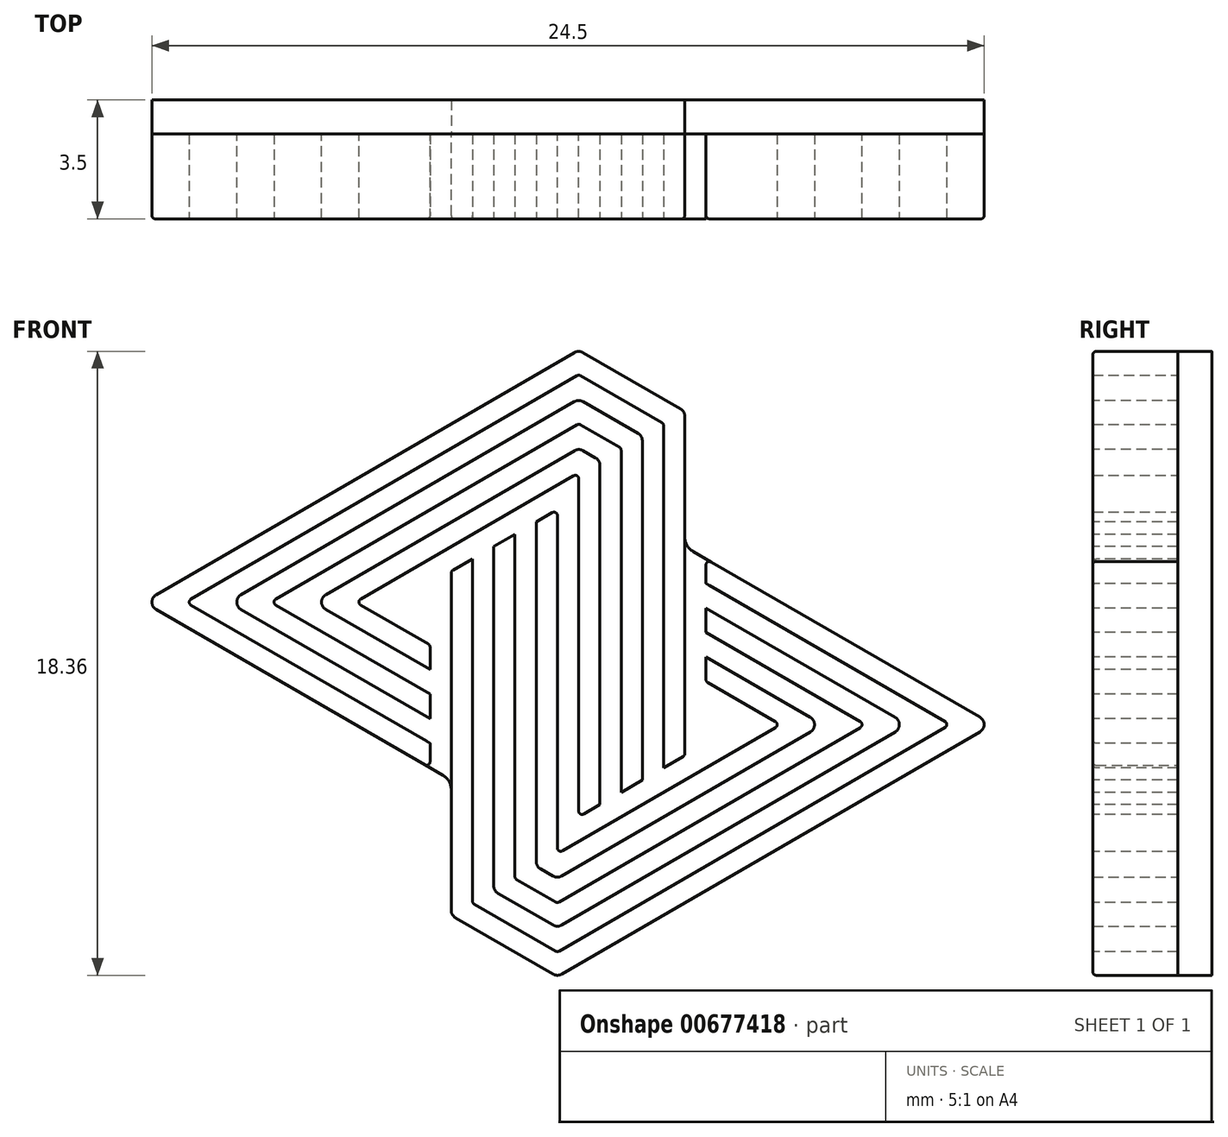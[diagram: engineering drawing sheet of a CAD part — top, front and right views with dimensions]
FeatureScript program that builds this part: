
annotation { "Feature Type Name" : "Feature", "Feature Type Description" : "" }
export const myFeature = defineFeature(function(context is Context, id is Id, definition is map)
    precondition{}
    {
        {
            var Q0;
            Q0=qCreatedBy(makeId("Front.planeOp"),FACE);
            var sketch = newSketch(context, id + "F0", { "sketchPlane" : qUnion([Q0])});
            skLineSegment(sketch, "E0.bottom", {"start": v(-12.5, 9.22) * mm, "end": v(12.5, 9.22) * mm, "construction": true});
            skLineSegment(sketch, "E0.top", {"start": v(-12.5, -9.22) * mm, "end": v(12.5, -9.22) * mm, "construction": true});
            skLineSegment(sketch, "E0.left", {"start": v(-12.5, 9.22) * mm, "end": v(-12.5, -9.22) * mm, "construction": true});
            skLineSegment(sketch, "E0.right", {"start": v(12.5, 9.22) * mm, "end": v(12.5, -9.22) * mm, "construction": true});
            skLineSegment(sketch, "E1", {"start": v(0, 9.22) * mm, "end": v(0, -9.22) * mm, "construction": true});
            skLineSegment(sketch, "E2", {"start": v(-3.44, 9.22) * mm, "end": v(-3.44, -9.22) * mm, "construction": true});
            skLineSegment(sketch, "E3.MirrorCS", {"start": v(3.44, 9.22) * mm, "end": v(3.44, -9.22) * mm, "construction": true});
            skLineSegment(sketch, "E4", {"start": v(-12.5, 1.8) * mm, "end": v(-3.44, 1.8) * mm, "construction": true});
            skLineSegment(sketch, "E5", {"start": v(3.44, -1.8) * mm, "end": v(12.5, -1.8) * mm, "construction": true});
            skLineSegment(sketch, "E6", {"start": v(-0.31, 0) * mm, "end": v(-0.31, -9.22) * mm, "construction": true});
            skLineSegment(sketch, "E7", {"start": v(-3.44, -7.42) * mm, "end": v(0, -7.42) * mm, "construction": true});
            skLineSegment(sketch, "E8", {"start": v(0, 7.42) * mm, "end": v(3.44, 7.42) * mm, "construction": true});
            skLineSegment(sketch, "E9", {"start": v(-4.06, -9.22) * mm, "end": v(-4.06, 1.8) * mm, "construction": true});
            skLineSegment(sketch, "E10", {"start": v(0.31, 0) * mm, "end": v(0.31, 9.22) * mm, "construction": true});
            skLineSegment(sketch, "E11", {"start": v(-12.5, 1.8) * mm, "end": v(0.31, 9.22) * mm});
            skLineSegment(sketch, "E12", {"start": v(0.31, 9.22) * mm, "end": v(3.44, 7.42) * mm});
            skLineSegment(sketch, "E13", {"start": v(-0.31, -9.22) * mm, "end": v(-3.44, -7.42) * mm});
            skLineSegment(sketch, "E14", {"start": v(-0.31, -9.22) * mm, "end": v(12.5, -1.8) * mm});
            skLineSegment(sketch, "E15", {"start": v(-12.5, 1.8) * mm, "end": v(-4.06, -3.07) * mm});
            skLineSegment(sketch, "E16", {"start": v(-3.44, -7.42) * mm, "end": v(-3.44, 1.8) * mm});
            skLineSegment(sketch, "E17.MirrorCS", {"start": v(4.06, -9.22) * mm, "end": v(4.06, 1.8) * mm, "construction": true});
            skLineSegment(sketch, "E18", {"start": v(4.06, 1.8) * mm, "end": v(4.06, 5.32) * mm, "construction": true});
            skLineSegment(sketch, "E19", {"start": v(12.5, -1.8) * mm, "end": v(4.06, 3.07) * mm});
            skLineSegment(sketch, "E20.0", {"start": v(-6.26, 1.8) * mm, "end": v(-4.06, 0.54) * mm});
            skLineSegment(sketch, "E21.trimOffspring", {"start": v(-6.26, 1.8) * mm, "end": v(0.31, 5.6) * mm});
            skLineSegment(sketch, "E22.0", {"start": v(6.26, -1.8) * mm, "end": v(4.06, -0.54) * mm});
            skLineSegment(sketch, "E22.1", {"start": v(-0.31, -5.6) * mm, "end": v(6.26, -1.8) * mm});
            skLineSegment(sketch, "E23", {"start": v(-2.2, 4.16) * mm, "end": v(-1.88, 3.62) * mm, "construction": true});
            skLineSegment(sketch, "E24.0", {"start": v(-3.44, 2.71) * mm, "end": v(-0.31, 4.52) * mm});
            skLineSegment(sketch, "E25", {"start": v(-3.44, 2.71) * mm, "end": v(-3.44, 1.8) * mm});
            skLineSegment(sketch, "E26.0", {"start": v(0.31, -4.52) * mm, "end": v(3.44, -2.71) * mm});
            skPoint(sketch, "E27.orphan", {"position": v(1.88, 6.51) * mm});
            skLineSegment(sketch, "E28", {"start": v(3.44, 7.42) * mm, "end": v(3.44, -2.71) * mm});
            skLineSegment(sketch, "E29", {"start": v(0.31, -4.52) * mm, "end": v(0.31, 5.6) * mm});
            skLineSegment(sketch, "E30", {"start": v(-0.31, 4.52) * mm, "end": v(-0.31, -5.6) * mm});
            skLineSegment(sketch, "E31", {"start": v(-4.06, -3.07) * mm, "end": v(-4.06, 0.54) * mm});
            skLineSegment(sketch, "E32", {"start": v(4.06, 3.07) * mm, "end": v(4.06, -0.54) * mm});
            skSolve(sketch);
        }
        {
            var Q0;
            Q0 = qSketchRegion(id + "F0", true);
            extrude(context, id + "F1", {"entities" : qUnion([Q0]), "depth" : 2.5 * mm, "offsetDistance" : 25 * mm});
        }
        {
            var Q0;
            Q0=makeQuery(id+"F1.opExtrude","CAP_FACE",FACE,{"disambiguationData":[OSD([sQuery(id+"F0.wireOp",EDGE,"E11"),sQuery(id+"F0.wireOp",EDGE,"E12"),sQuery(id+"F0.wireOp",EDGE,"E15"),sQuery(id+"F0.wireOp",EDGE,"E20.0"),sQuery(id+"F0.wireOp",EDGE,"E21.trimOffspring"),sQuery(id+"F0.wireOp",EDGE,"E26.0"),sQuery(id+"F0.wireOp",EDGE,"E28"),sQuery(id+"F0.wireOp",EDGE,"E29"),sQuery(id+"F0.wireOp",EDGE,"E31")])],"isStart":false});
            var sketch = newSketch(context, id + "F2", { "sketchPlane" : qUnion([Q0])});
            skLineSegment(sketch, "E33.0", {"start": v(-11.25, 1.8) * mm, "end": v(-4.06, -2.35) * mm});
            skLineSegment(sketch, "E34.0", {"start": v(-11.25, 1.8) * mm, "end": v(0.31, 8.5) * mm});
            skLineSegment(sketch, "E35.0", {"start": v(2.81, 7.06) * mm, "end": v(2.81, -3.08) * mm});
            skLineSegment(sketch, "E35.1", {"start": v(0.31, 8.5) * mm, "end": v(2.81, 7.06) * mm});
            skLineSegment(sketch, "E36.0", {"start": v(-10, 1.8) * mm, "end": v(-4.06, -1.63) * mm});
            skLineSegment(sketch, "E36.1", {"start": v(-10, 1.8) * mm, "end": v(0.31, 7.78) * mm});
            skLineSegment(sketch, "E36.2", {"start": v(0.31, 7.78) * mm, "end": v(2.19, 6.7) * mm});
            skLineSegment(sketch, "E36.3", {"start": v(2.19, 6.7) * mm, "end": v(2.19, -3.44) * mm});
            skLineSegment(sketch, "E37", {"start": v(-4.06, -2.35) * mm, "end": v(-4.06, -1.63) * mm});
            skLineSegment(sketch, "E38", {"start": v(2.19, -3.44) * mm, "end": v(2.81, -3.08) * mm});
            skLineSegment(sketch, "E39.0", {"start": v(-8.75, 1.8) * mm, "end": v(-4.06, -0.9) * mm});
            skLineSegment(sketch, "E39.1", {"start": v(-8.75, 1.8) * mm, "end": v(0.32, 7.05) * mm});
            skLineSegment(sketch, "E39.2", {"start": v(0.32, 7.05) * mm, "end": v(1.56, 6.34) * mm});
            skLineSegment(sketch, "E39.3", {"start": v(1.56, 6.34) * mm, "end": v(1.56, -3.8) * mm});
            skLineSegment(sketch, "E40.0", {"start": v(-7.5, 1.8) * mm, "end": v(-4.06, -0.18) * mm});
            skLineSegment(sketch, "E40.1", {"start": v(-7.5, 1.8) * mm, "end": v(0.32, 6.33) * mm});
            skLineSegment(sketch, "E40.2", {"start": v(0.32, 6.33) * mm, "end": v(0.94, 5.97) * mm});
            skLineSegment(sketch, "E40.3", {"start": v(0.94, 5.97) * mm, "end": v(0.94, -4.16) * mm});
            skLineSegment(sketch, "E41", {"start": v(-4.06, -0.9) * mm, "end": v(-4.06, -0.18) * mm});
            skLineSegment(sketch, "E42", {"start": v(0.94, -4.16) * mm, "end": v(1.56, -3.8) * mm});
            skSolve(sketch);
        }
        {
            var Q0;
            Q0 = qSketchRegion(id + "F2", true);
            extrude(context, id + "F3", {"entities" : qUnion([Q0]), "operationType" : NewBodyOperationType.REMOVE, "oppositeDirection" : true, "depth" : 25 * mm, "offsetDistance" : 25 * mm});
        }
        {
            var Q0;
            Q0=makeQuery(id+"F1.opExtrude","CAP_FACE",FACE,{"disambiguationData":[OSD([sQuery(id+"F0.wireOp",EDGE,"E13"),sQuery(id+"F0.wireOp",EDGE,"E14"),sQuery(id+"F0.wireOp",EDGE,"E16"),sQuery(id+"F0.wireOp",EDGE,"E19"),sQuery(id+"F0.wireOp",EDGE,"E22.0"),sQuery(id+"F0.wireOp",EDGE,"E22.1"),sQuery(id+"F0.wireOp",EDGE,"E24.0"),sQuery(id+"F0.wireOp",EDGE,"E25"),sQuery(id+"F0.wireOp",EDGE,"E30"),sQuery(id+"F0.wireOp",EDGE,"E32")])],"isStart":false});
            var sketch = newSketch(context, id + "F4", { "sketchPlane" : qUnion([Q0])});
            skLineSegment(sketch, "E43.0", {"start": v(11.25, -1.8) * mm, "end": v(4.06, 2.35) * mm});
            skLineSegment(sketch, "E43.1", {"start": v(-2.81, 3.08) * mm, "end": v(-2.81, 1.8) * mm});
            skLineSegment(sketch, "E43.2", {"start": v(-2.81, -7.06) * mm, "end": v(-2.81, 1.8) * mm});
            skLineSegment(sketch, "E43.3", {"start": v(-0.31, -8.5) * mm, "end": v(-2.81, -7.06) * mm});
            skLineSegment(sketch, "E43.4", {"start": v(-0.31, -8.5) * mm, "end": v(11.25, -1.8) * mm});
            skLineSegment(sketch, "E44.0", {"start": v(10, -1.8) * mm, "end": v(4.06, 1.63) * mm});
            skLineSegment(sketch, "E44.1", {"start": v(-2.19, 3.44) * mm, "end": v(-2.19, 1.8) * mm});
            skLineSegment(sketch, "E44.2", {"start": v(-2.19, -6.7) * mm, "end": v(-2.19, 1.8) * mm});
            skLineSegment(sketch, "E44.3", {"start": v(-0.31, -7.78) * mm, "end": v(-2.19, -6.7) * mm});
            skLineSegment(sketch, "E44.4", {"start": v(-0.31, -7.78) * mm, "end": v(10, -1.8) * mm});
            skLineSegment(sketch, "E45", {"start": v(-2.81, 3.08) * mm, "end": v(-2.19, 3.44) * mm});
            skLineSegment(sketch, "E46", {"start": v(4.06, 1.63) * mm, "end": v(4.06, 2.35) * mm});
            skLineSegment(sketch, "E47.0", {"start": v(8.75, -1.8) * mm, "end": v(4.06, 0.9) * mm});
            skLineSegment(sketch, "E47.1", {"start": v(-1.56, 3.8) * mm, "end": v(-1.56, 1.8) * mm});
            skLineSegment(sketch, "E47.2", {"start": v(-1.56, -6.33) * mm, "end": v(-1.56, 1.8) * mm});
            skLineSegment(sketch, "E47.3", {"start": v(-0.31, -7.05) * mm, "end": v(-1.56, -6.33) * mm});
            skLineSegment(sketch, "E47.4", {"start": v(-0.31, -7.05) * mm, "end": v(8.75, -1.8) * mm});
            skLineSegment(sketch, "E48.0", {"start": v(7.5, -1.8) * mm, "end": v(4.06, 0.18) * mm});
            skLineSegment(sketch, "E48.1", {"start": v(-0.94, 4.16) * mm, "end": v(-0.94, 1.8) * mm});
            skLineSegment(sketch, "E48.2", {"start": v(-0.94, -5.97) * mm, "end": v(-0.94, 1.8) * mm});
            skLineSegment(sketch, "E48.3", {"start": v(-0.32, -6.33) * mm, "end": v(-0.94, -5.97) * mm});
            skLineSegment(sketch, "E48.4", {"start": v(-0.32, -6.33) * mm, "end": v(7.5, -1.8) * mm});
            skLineSegment(sketch, "E49", {"start": v(-1.56, 3.8) * mm, "end": v(-0.94, 4.16) * mm});
            skLineSegment(sketch, "E50", {"start": v(4.06, 0.18) * mm, "end": v(4.06, 0.9) * mm});
            skSolve(sketch);
        }
        {
            var Q0;
            Q0 = qSketchRegion(id + "F4", true);
            extrude(context, id + "F5", {"entities" : qUnion([Q0]), "operationType" : NewBodyOperationType.REMOVE, "oppositeDirection" : true, "depth" : 25 * mm, "offsetDistance" : 25 * mm});
        }
        {
            var Q0;
            {var subQ0=sQuery(id+"F0.wireOp",EDGE,"E19");var subQ1=sQuery(id+"F0.wireOp",EDGE,"E32");var subQ2=sQuery(id+"F0.wireOp",EDGE,"E14");var subQ3=sQuery(id+"F0.wireOp",EDGE,"E25");var subQ4=sQuery(id+"F0.wireOp",EDGE,"E16");var subQ5=sQuery(id+"F0.wireOp",EDGE,"E13");var subQ6=sQuery(id+"F0.wireOp",EDGE,"E24.0");Q0=makeQuery(id+"F5.boolean.opBoolean","SPLIT",FACE,{"disambiguationData":[TD([makeQuery(id+"F1.opExtrude","SWEPT_FACE",FACE,{"disambiguationData":[OSD([subQ5])]})])],"derivedFrom":makeQuery(id+"F1.opExtrude","CAP_FACE",FACE,{"disambiguationData":[OSD([subQ5,subQ2,subQ4,subQ0,sQuery(id+"F0.wireOp",EDGE,"E22.0"),sQuery(id+"F0.wireOp",EDGE,"E22.1"),subQ6,subQ3,sQuery(id+"F0.wireOp",EDGE,"E30"),subQ1])],"isStart":true})});}
            var sketch = newSketch(context, id + "F6", { "sketchPlane" : qUnion([Q0])});
            skLineSegment(sketch, "E51.0", {"start": v(-12.5, -1.8) * mm, "end": v(-4.06, 3.07) * mm});
            skLineSegment(sketch, "E51.1", {"start": v(0.31, -9.22) * mm, "end": v(-12.5, -1.8) * mm});
            skLineSegment(sketch, "E51.2", {"start": v(0.31, -9.22) * mm, "end": v(3.44, -7.42) * mm});
            skLineSegment(sketch, "E51.3", {"start": v(3.44, -3.43) * mm, "end": v(3.44, -7.42) * mm});
            skLineSegment(sketch, "E51.4", {"start": v(12.5, 1.8) * mm, "end": v(4.06, -3.07) * mm});
            skLineSegment(sketch, "E51.5", {"start": v(-3.44, 7.42) * mm, "end": v(-3.44, 3.43) * mm});
            skLineSegment(sketch, "E51.6", {"start": v(-0.31, 9.22) * mm, "end": v(-3.44, 7.42) * mm});
            skLineSegment(sketch, "E51.7", {"start": v(12.5, 1.8) * mm, "end": v(-0.31, 9.22) * mm});
            skPoint(sketch, "E51.8", {"position": v(1.87, -8.32) * mm});
            skLineSegment(sketch, "E52", {"start": v(-4.06, 3.07) * mm, "end": v(-3.44, 3.43) * mm});
            skLineSegment(sketch, "E53", {"start": v(4.06, -3.07) * mm, "end": v(3.44, -3.43) * mm});
            skPoint(sketch, "E54.orphan", {"position": v(-3.44, -2.71) * mm});
            skPoint(sketch, "E55.orphan", {"position": v(3.44, 2.71) * mm});
            skSolve(sketch);
        }
        {
            var Q0;
            Q0 = qSketchRegion(id + "F6", true);
            extrude(context, id + "F7", {"entities" : qUnion([Q0]), "depth" : 1 * mm, "offsetDistance" : 25 * mm});
        }
        {
            var Q0;
            Q0=makeQuery(id+"F1.opExtrude","SWEPT_EDGE",EDGE,{"disambiguationData":[OSD([sQuery(id+"F0.wireOp",EDGE,"E11"),sQuery(id+"F0.wireOp",EDGE,"E15")])]});
            var Q1;
            Q1=makeQuery(id+"F1.opExtrude","SWEPT_EDGE",EDGE,{"disambiguationData":[OSD([sQuery(id+"F0.wireOp",EDGE,"E14"),sQuery(id+"F0.wireOp",EDGE,"E19")])]});
            var Q2;
            Q2=makeQuery(id+"F7.opExtrude","SWEPT_EDGE",EDGE,{"disambiguationData":[OSD([sQuery(id+"F6.wireOp",EDGE,"E51.0"),sQuery(id+"F6.wireOp",EDGE,"E51.1")])]});
            var Q3;
            Q3=makeQuery(id+"F7.opExtrude","SWEPT_EDGE",EDGE,{"disambiguationData":[OSD([sQuery(id+"F6.wireOp",EDGE,"E51.4"),sQuery(id+"F6.wireOp",EDGE,"E51.7")])]});
            var Q4;
            Q4=makeQuery(id+"F1.opExtrude","SWEPT_EDGE",EDGE,{"disambiguationData":[OSD([sQuery(id+"F0.wireOp",EDGE,"E11"),sQuery(id+"F0.wireOp",EDGE,"E12")])]});
            var Q5;
            Q5=makeQuery(id+"F7.opExtrude","SWEPT_EDGE",EDGE,{"disambiguationData":[OSD([sQuery(id+"F6.wireOp",EDGE,"E51.6"),sQuery(id+"F6.wireOp",EDGE,"E51.7")])]});
            var Q6;
            Q6=makeQuery(id+"F1.opExtrude","SWEPT_EDGE",EDGE,{"disambiguationData":[OSD([sQuery(id+"F0.wireOp",EDGE,"E12"),sQuery(id+"F0.wireOp",EDGE,"E28")])]});
            var Q7;
            Q7=makeQuery(id+"F7.opExtrude","SWEPT_EDGE",EDGE,{"disambiguationData":[OSD([sQuery(id+"F6.wireOp",EDGE,"E51.5"),sQuery(id+"F6.wireOp",EDGE,"E51.6")])]});
            var Q8;
            Q8=makeQuery(id+"F1.opExtrude","SWEPT_EDGE",EDGE,{"disambiguationData":[OSD([sQuery(id+"F0.wireOp",EDGE,"E13"),sQuery(id+"F0.wireOp",EDGE,"E16")])]});
            var Q9;
            Q9=makeQuery(id+"F7.opExtrude","SWEPT_EDGE",EDGE,{"disambiguationData":[OSD([sQuery(id+"F6.wireOp",EDGE,"E51.2"),sQuery(id+"F6.wireOp",EDGE,"E51.3")])]});
            var Q10;
            Q10=makeQuery(id+"F1.opExtrude","SWEPT_EDGE",EDGE,{"disambiguationData":[OSD([sQuery(id+"F0.wireOp",EDGE,"E13"),sQuery(id+"F0.wireOp",EDGE,"E14")])]});
            var Q11;
            Q11=makeQuery(id+"F7.opExtrude","SWEPT_EDGE",EDGE,{"disambiguationData":[OSD([sQuery(id+"F6.wireOp",EDGE,"E51.1"),sQuery(id+"F6.wireOp",EDGE,"E51.2")])]});
            var Q12;
            Q12=makeQuery(id+"F5.boolean.opBoolean","COPY",EDGE,{"derivedFrom":makeQuery(id+"F5.opExtrude","SWEPT_EDGE",EDGE,{"disambiguationData":[OSD([sQuery(id+"F4.wireOp",EDGE,"E44.2"),sQuery(id+"F4.wireOp",EDGE,"E44.3")])]})});
            var Q13;
            Q13=makeQuery(id+"F5.boolean.opBoolean","COPY",EDGE,{"derivedFrom":makeQuery(id+"F5.opExtrude","SWEPT_EDGE",EDGE,{"disambiguationData":[OSD([sQuery(id+"F4.wireOp",EDGE,"E44.3"),sQuery(id+"F4.wireOp",EDGE,"E44.4")])]})});
            var Q14;
            Q14=makeQuery(id+"F5.boolean.opBoolean","COPY",EDGE,{"derivedFrom":makeQuery(id+"F5.opExtrude","SWEPT_EDGE",EDGE,{"disambiguationData":[OSD([sQuery(id+"F4.wireOp",EDGE,"E48.2"),sQuery(id+"F4.wireOp",EDGE,"E48.3")])]})});
            var Q15;
            Q15=makeQuery(id+"F5.boolean.opBoolean","COPY",EDGE,{"derivedFrom":makeQuery(id+"F5.opExtrude","SWEPT_EDGE",EDGE,{"disambiguationData":[OSD([sQuery(id+"F4.wireOp",EDGE,"E48.3"),sQuery(id+"F4.wireOp",EDGE,"E48.4")])]})});
            var Q16;
            Q16=makeQuery(id+"F3.boolean.opBoolean","COPY",EDGE,{"derivedFrom":makeQuery(id+"F3.opExtrude","SWEPT_EDGE",EDGE,{"disambiguationData":[OSD([sQuery(id+"F2.wireOp",EDGE,"E40.1"),sQuery(id+"F2.wireOp",EDGE,"E40.2")])]})});
            var Q17;
            Q17=makeQuery(id+"F3.boolean.opBoolean","COPY",EDGE,{"derivedFrom":makeQuery(id+"F3.opExtrude","SWEPT_EDGE",EDGE,{"disambiguationData":[OSD([sQuery(id+"F2.wireOp",EDGE,"E40.2"),sQuery(id+"F2.wireOp",EDGE,"E40.3")])]})});
            var Q18;
            Q18=makeQuery(id+"F3.boolean.opBoolean","COPY",EDGE,{"derivedFrom":makeQuery(id+"F3.opExtrude","SWEPT_EDGE",EDGE,{"disambiguationData":[OSD([sQuery(id+"F2.wireOp",EDGE,"E36.2"),sQuery(id+"F2.wireOp",EDGE,"E36.3")])]})});
            var Q19;
            Q19=makeQuery(id+"F3.boolean.opBoolean","COPY",EDGE,{"derivedFrom":makeQuery(id+"F3.opExtrude","SWEPT_EDGE",EDGE,{"disambiguationData":[OSD([sQuery(id+"F2.wireOp",EDGE,"E36.1"),sQuery(id+"F2.wireOp",EDGE,"E36.2")])]})});
            var Q20;
            Q20=makeQuery(id+"F3.boolean.opBoolean","COPY",EDGE,{"derivedFrom":makeQuery(id+"F3.opExtrude","SWEPT_EDGE",EDGE,{"disambiguationData":[OSD([sQuery(id+"F2.wireOp",EDGE,"E36.0"),sQuery(id+"F2.wireOp",EDGE,"E36.1")])]})});
            var Q21;
            Q21=makeQuery(id+"F3.boolean.opBoolean","COPY",EDGE,{"derivedFrom":makeQuery(id+"F3.opExtrude","SWEPT_EDGE",EDGE,{"disambiguationData":[OSD([sQuery(id+"F2.wireOp",EDGE,"E40.0"),sQuery(id+"F2.wireOp",EDGE,"E40.1")])]})});
            var Q22;
            Q22=makeQuery(id+"F5.boolean.opBoolean","COPY",EDGE,{"derivedFrom":makeQuery(id+"F5.opExtrude","SWEPT_EDGE",EDGE,{"disambiguationData":[OSD([sQuery(id+"F4.wireOp",EDGE,"E44.0"),sQuery(id+"F4.wireOp",EDGE,"E44.4")])]})});
            var Q23;
            Q23=makeQuery(id+"F5.boolean.opBoolean","COPY",EDGE,{"derivedFrom":makeQuery(id+"F5.opExtrude","SWEPT_EDGE",EDGE,{"disambiguationData":[OSD([sQuery(id+"F4.wireOp",EDGE,"E48.0"),sQuery(id+"F4.wireOp",EDGE,"E48.4")])]})});
            fillet(context, id + "F8", {"entities" : qUnion([Q0, Q1, Q2, Q3, Q4, Q5, Q6, Q7, Q8, Q9, Q10, Q11, Q12, Q13, Q14, Q15, Q16, Q17, Q18, Q19, Q20, Q21, Q22, Q23]), "radius" : 0.25 * mm, "tangentPropagation" : true, "allowEdgeOverflow" : false});
        }
        {
            var Q0;
            Q0=makeQuery(id+"F5.boolean.opBoolean","COPY",EDGE,{"derivedFrom":makeQuery(id+"F5.opExtrude","SWEPT_EDGE",EDGE,{"disambiguationData":[OSD([sQuery(id+"F4.wireOp",EDGE,"E43.3"),sQuery(id+"F4.wireOp",EDGE,"E43.4")])]})});
            var Q1;
            Q1=makeQuery(id+"F5.boolean.opBoolean","COPY",EDGE,{"derivedFrom":makeQuery(id+"F5.opExtrude","SWEPT_EDGE",EDGE,{"disambiguationData":[OSD([sQuery(id+"F4.wireOp",EDGE,"E43.2"),sQuery(id+"F4.wireOp",EDGE,"E43.3")])]})});
            var Q2;
            Q2=makeQuery(id+"F5.boolean.opBoolean","COPY",EDGE,{"derivedFrom":makeQuery(id+"F5.opExtrude","SWEPT_EDGE",EDGE,{"disambiguationData":[OSD([sQuery(id+"F4.wireOp",EDGE,"E47.3"),sQuery(id+"F4.wireOp",EDGE,"E47.4")])]})});
            var Q3;
            Q3=makeQuery(id+"F5.boolean.opBoolean","COPY",EDGE,{"derivedFrom":makeQuery(id+"F5.opExtrude","SWEPT_EDGE",EDGE,{"disambiguationData":[OSD([sQuery(id+"F4.wireOp",EDGE,"E47.2"),sQuery(id+"F4.wireOp",EDGE,"E47.3")])]})});
            var Q4;
            Q4=makeQuery(id+"F1.opExtrude","SWEPT_EDGE",EDGE,{"disambiguationData":[OSD([sQuery(id+"F0.wireOp",EDGE,"E22.1"),sQuery(id+"F0.wireOp",EDGE,"E30")])]});
            var Q5;
            Q5=makeQuery(id+"F1.opExtrude","SWEPT_EDGE",EDGE,{"disambiguationData":[OSD([sQuery(id+"F0.wireOp",EDGE,"E22.0"),sQuery(id+"F0.wireOp",EDGE,"E22.1")])]});
            var Q6;
            Q6=makeQuery(id+"F5.boolean.opBoolean","COPY",EDGE,{"derivedFrom":makeQuery(id+"F5.opExtrude","SWEPT_EDGE",EDGE,{"disambiguationData":[OSD([sQuery(id+"F4.wireOp",EDGE,"E47.0"),sQuery(id+"F4.wireOp",EDGE,"E47.4")])]})});
            var Q7;
            Q7=makeQuery(id+"F5.boolean.opBoolean","COPY",EDGE,{"derivedFrom":makeQuery(id+"F5.opExtrude","SWEPT_EDGE",EDGE,{"disambiguationData":[OSD([sQuery(id+"F4.wireOp",EDGE,"E43.0"),sQuery(id+"F4.wireOp",EDGE,"E43.4")])]})});
            var Q8;
            Q8=makeQuery(id+"F1.opExtrude","SWEPT_EDGE",EDGE,{"disambiguationData":[OSD([sQuery(id+"F0.wireOp",EDGE,"E21.trimOffspring"),sQuery(id+"F0.wireOp",EDGE,"E29")])]});
            var Q9;
            Q9=makeQuery(id+"F3.boolean.opBoolean","COPY",EDGE,{"derivedFrom":makeQuery(id+"F3.opExtrude","SWEPT_EDGE",EDGE,{"disambiguationData":[OSD([sQuery(id+"F2.wireOp",EDGE,"E39.1"),sQuery(id+"F2.wireOp",EDGE,"E39.2")])]})});
            var Q10;
            Q10=makeQuery(id+"F3.boolean.opBoolean","COPY",EDGE,{"derivedFrom":makeQuery(id+"F3.opExtrude","SWEPT_EDGE",EDGE,{"disambiguationData":[OSD([sQuery(id+"F2.wireOp",EDGE,"E39.2"),sQuery(id+"F2.wireOp",EDGE,"E39.3")])]})});
            var Q11;
            Q11=makeQuery(id+"F3.boolean.opBoolean","COPY",EDGE,{"derivedFrom":makeQuery(id+"F3.opExtrude","SWEPT_EDGE",EDGE,{"disambiguationData":[OSD([sQuery(id+"F2.wireOp",EDGE,"E35.0"),sQuery(id+"F2.wireOp",EDGE,"E35.1")])]})});
            var Q12;
            Q12=makeQuery(id+"F3.boolean.opBoolean","COPY",EDGE,{"derivedFrom":makeQuery(id+"F3.opExtrude","SWEPT_EDGE",EDGE,{"disambiguationData":[OSD([sQuery(id+"F2.wireOp",EDGE,"E34.0"),sQuery(id+"F2.wireOp",EDGE,"E35.1")])]})});
            var Q13;
            Q13=makeQuery(id+"F3.boolean.opBoolean","COPY",EDGE,{"derivedFrom":makeQuery(id+"F3.opExtrude","SWEPT_EDGE",EDGE,{"disambiguationData":[OSD([sQuery(id+"F2.wireOp",EDGE,"E33.0"),sQuery(id+"F2.wireOp",EDGE,"E34.0")])]})});
            var Q14;
            Q14=makeQuery(id+"F3.boolean.opBoolean","COPY",EDGE,{"derivedFrom":makeQuery(id+"F3.opExtrude","SWEPT_EDGE",EDGE,{"disambiguationData":[OSD([sQuery(id+"F2.wireOp",EDGE,"E39.0"),sQuery(id+"F2.wireOp",EDGE,"E39.1")])]})});
            var Q15;
            Q15=makeQuery(id+"F1.opExtrude","SWEPT_EDGE",EDGE,{"disambiguationData":[OSD([sQuery(id+"F0.wireOp",EDGE,"E20.0"),sQuery(id+"F0.wireOp",EDGE,"E21.trimOffspring")])]});
            var Q16;
            Q16=makeQuery(id+"F1.opExtrude","SWEPT_EDGE",EDGE,{"disambiguationData":[OSD([sQuery(id+"F0.wireOp",EDGE,"E22.0"),sQuery(id+"F0.wireOp",EDGE,"E32")])]});
            var Q17;
            Q17=makeQuery(id+"F5.boolean.opBoolean","COPY",EDGE,{"derivedFrom":makeQuery(id+"F5.opExtrude","SWEPT_EDGE",EDGE,{"disambiguationData":[OSD([sQuery(id+"F0.wireOp",EDGE,"E32"),sQuery(id+"F4.wireOp",EDGE,"E48.0"),sQuery(id+"F4.wireOp",EDGE,"E50")])]})});
            var Q18;
            Q18=makeQuery(id+"F5.boolean.opBoolean","COPY",EDGE,{"derivedFrom":makeQuery(id+"F5.opExtrude","SWEPT_EDGE",EDGE,{"disambiguationData":[OSD([sQuery(id+"F0.wireOp",EDGE,"E32"),sQuery(id+"F4.wireOp",EDGE,"E47.0"),sQuery(id+"F4.wireOp",EDGE,"E50")])]})});
            var Q19;
            Q19=makeQuery(id+"F5.boolean.opBoolean","COPY",EDGE,{"derivedFrom":makeQuery(id+"F5.opExtrude","SWEPT_EDGE",EDGE,{"disambiguationData":[OSD([sQuery(id+"F0.wireOp",EDGE,"E32"),sQuery(id+"F4.wireOp",EDGE,"E44.0"),sQuery(id+"F4.wireOp",EDGE,"E46")])]})});
            var Q20;
            Q20=makeQuery(id+"F5.boolean.opBoolean","COPY",EDGE,{"derivedFrom":makeQuery(id+"F5.opExtrude","SWEPT_EDGE",EDGE,{"disambiguationData":[OSD([sQuery(id+"F0.wireOp",EDGE,"E32"),sQuery(id+"F4.wireOp",EDGE,"E43.0"),sQuery(id+"F4.wireOp",EDGE,"E46")])]})});
            var Q21;
            Q21=makeQuery(id+"F1.opExtrude","SWEPT_EDGE",EDGE,{"disambiguationData":[OSD([sQuery(id+"F0.wireOp",EDGE,"E19"),sQuery(id+"F0.wireOp",EDGE,"E32")])]});
            var Q22;
            Q22=makeQuery(id+"F1.opExtrude","SWEPT_EDGE",EDGE,{"disambiguationData":[OSD([sQuery(id+"F0.wireOp",EDGE,"E26.0"),sQuery(id+"F0.wireOp",EDGE,"E28")])]});
            var Q23;
            Q23=makeQuery(id+"F3.boolean.opBoolean","COPY",EDGE,{"derivedFrom":makeQuery(id+"F3.opExtrude","SWEPT_EDGE",EDGE,{"disambiguationData":[OSD([sQuery(id+"F0.wireOp",EDGE,"E26.0"),sQuery(id+"F2.wireOp",EDGE,"E35.0"),sQuery(id+"F2.wireOp",EDGE,"E38")])]})});
            var Q24;
            Q24=makeQuery(id+"F3.boolean.opBoolean","COPY",EDGE,{"derivedFrom":makeQuery(id+"F3.opExtrude","SWEPT_EDGE",EDGE,{"disambiguationData":[OSD([sQuery(id+"F0.wireOp",EDGE,"E26.0"),sQuery(id+"F2.wireOp",EDGE,"E36.3"),sQuery(id+"F2.wireOp",EDGE,"E38")])]})});
            var Q25;
            Q25=makeQuery(id+"F3.boolean.opBoolean","COPY",EDGE,{"derivedFrom":makeQuery(id+"F3.opExtrude","SWEPT_EDGE",EDGE,{"disambiguationData":[OSD([sQuery(id+"F0.wireOp",EDGE,"E26.0"),sQuery(id+"F2.wireOp",EDGE,"E39.3"),sQuery(id+"F2.wireOp",EDGE,"E42")])]})});
            var Q26;
            Q26=makeQuery(id+"F3.boolean.opBoolean","COPY",EDGE,{"derivedFrom":makeQuery(id+"F3.opExtrude","SWEPT_EDGE",EDGE,{"disambiguationData":[OSD([sQuery(id+"F0.wireOp",EDGE,"E26.0"),sQuery(id+"F2.wireOp",EDGE,"E40.3"),sQuery(id+"F2.wireOp",EDGE,"E42")])]})});
            var Q27;
            Q27=makeQuery(id+"F1.opExtrude","SWEPT_EDGE",EDGE,{"disambiguationData":[OSD([sQuery(id+"F0.wireOp",EDGE,"E26.0"),sQuery(id+"F0.wireOp",EDGE,"E29")])]});
            var Q28;
            Q28=makeQuery(id+"F1.opExtrude","SWEPT_EDGE",EDGE,{"disambiguationData":[OSD([sQuery(id+"F0.wireOp",EDGE,"E24.0"),sQuery(id+"F0.wireOp",EDGE,"E25")])]});
            var Q29;
            Q29=makeQuery(id+"F5.boolean.opBoolean","COPY",EDGE,{"derivedFrom":makeQuery(id+"F5.opExtrude","SWEPT_EDGE",EDGE,{"disambiguationData":[OSD([sQuery(id+"F0.wireOp",EDGE,"E24.0"),sQuery(id+"F4.wireOp",EDGE,"E44.1"),sQuery(id+"F4.wireOp",EDGE,"E45")])]})});
            var Q30;
            Q30=makeQuery(id+"F5.boolean.opBoolean","COPY",EDGE,{"derivedFrom":makeQuery(id+"F5.opExtrude","SWEPT_EDGE",EDGE,{"disambiguationData":[OSD([sQuery(id+"F0.wireOp",EDGE,"E24.0"),sQuery(id+"F4.wireOp",EDGE,"E47.1"),sQuery(id+"F4.wireOp",EDGE,"E49")])]})});
            var Q31;
            Q31=makeQuery(id+"F1.opExtrude","SWEPT_EDGE",EDGE,{"disambiguationData":[OSD([sQuery(id+"F0.wireOp",EDGE,"E24.0"),sQuery(id+"F0.wireOp",EDGE,"E30")])]});
            var Q32;
            Q32=makeQuery(id+"F5.boolean.opBoolean","COPY",EDGE,{"derivedFrom":makeQuery(id+"F5.opExtrude","SWEPT_EDGE",EDGE,{"disambiguationData":[OSD([sQuery(id+"F0.wireOp",EDGE,"E24.0"),sQuery(id+"F4.wireOp",EDGE,"E48.1"),sQuery(id+"F4.wireOp",EDGE,"E49")])]})});
            var Q33;
            Q33=makeQuery(id+"F5.boolean.opBoolean","COPY",EDGE,{"derivedFrom":makeQuery(id+"F5.opExtrude","SWEPT_EDGE",EDGE,{"disambiguationData":[OSD([sQuery(id+"F0.wireOp",EDGE,"E24.0"),sQuery(id+"F4.wireOp",EDGE,"E43.1"),sQuery(id+"F4.wireOp",EDGE,"E45")])]})});
            var Q34;
            Q34=makeQuery(id+"F1.opExtrude","SWEPT_EDGE",EDGE,{"disambiguationData":[OSD([sQuery(id+"F0.wireOp",EDGE,"E20.0"),sQuery(id+"F0.wireOp",EDGE,"E31")])]});
            var Q35;
            Q35=makeQuery(id+"F3.boolean.opBoolean","COPY",EDGE,{"derivedFrom":makeQuery(id+"F3.opExtrude","SWEPT_EDGE",EDGE,{"disambiguationData":[OSD([sQuery(id+"F0.wireOp",EDGE,"E31"),sQuery(id+"F2.wireOp",EDGE,"E39.0"),sQuery(id+"F2.wireOp",EDGE,"E41")])]})});
            var Q36;
            Q36=makeQuery(id+"F3.boolean.opBoolean","COPY",EDGE,{"derivedFrom":makeQuery(id+"F3.opExtrude","SWEPT_EDGE",EDGE,{"disambiguationData":[OSD([sQuery(id+"F0.wireOp",EDGE,"E31"),sQuery(id+"F2.wireOp",EDGE,"E33.0"),sQuery(id+"F2.wireOp",EDGE,"E37")])]})});
            var Q37;
            Q37=makeQuery(id+"F3.boolean.opBoolean","COPY",EDGE,{"derivedFrom":makeQuery(id+"F3.opExtrude","SWEPT_EDGE",EDGE,{"disambiguationData":[OSD([sQuery(id+"F0.wireOp",EDGE,"E31"),sQuery(id+"F2.wireOp",EDGE,"E40.0"),sQuery(id+"F2.wireOp",EDGE,"E41")])]})});
            var Q38;
            Q38=makeQuery(id+"F3.boolean.opBoolean","COPY",EDGE,{"derivedFrom":makeQuery(id+"F3.opExtrude","SWEPT_EDGE",EDGE,{"disambiguationData":[OSD([sQuery(id+"F0.wireOp",EDGE,"E31"),sQuery(id+"F2.wireOp",EDGE,"E36.0"),sQuery(id+"F2.wireOp",EDGE,"E37")])]})});
            var Q39;
            Q39=makeQuery(id+"F1.opExtrude","SWEPT_EDGE",EDGE,{"disambiguationData":[OSD([sQuery(id+"F0.wireOp",EDGE,"E15"),sQuery(id+"F0.wireOp",EDGE,"E31")])]});
            fillet(context, id + "F9", {"entities" : qUnion([Q0, Q1, Q2, Q3, Q4, Q5, Q6, Q7, Q8, Q9, Q10, Q11, Q12, Q13, Q14, Q15, Q16, Q17, Q18, Q19, Q20, Q21, Q22, Q23, Q24, Q25, Q26, Q27, Q28, Q29, Q30, Q31, Q32, Q33, Q34, Q35, Q36, Q37, Q38, Q39]), "radius" : 0.1 * mm, "tangentPropagation" : true, "allowEdgeOverflow" : false});
        }
        {
            var Q0;
            Q0=makeQuery(id+"F1.opExtrude","CAP_EDGE",EDGE,{"disambiguationData":[OSD([sQuery(id+"F0.wireOp",EDGE,"E19")])],"isStart":false});
            var Q1;
            Q1=makeQuery(id+"F5.boolean.opBoolean","COPY",EDGE,{"derivedFrom":makeQuery(id+"F5.opExtrude","CAP_EDGE",EDGE,{"disambiguationData":[OSD([sQuery(id+"F4.wireOp",EDGE,"E44.0")])],"isStart":true})});
            var Q2;
            Q2=makeQuery(id+"F5.boolean.opBoolean","COPY",EDGE,{"derivedFrom":makeQuery(id+"F5.opExtrude","CAP_EDGE",EDGE,{"disambiguationData":[OSD([sQuery(id+"F4.wireOp",EDGE,"E48.0")])],"isStart":true})});
            var Q3;
            Q3=makeQuery(id+"F1.opExtrude","CAP_EDGE",EDGE,{"disambiguationData":[OSD([sQuery(id+"F0.wireOp",EDGE,"E28")])],"isStart":false});
            var Q4;
            Q4=makeQuery(id+"F3.boolean.opBoolean","COPY",EDGE,{"derivedFrom":makeQuery(id+"F3.opExtrude","CAP_EDGE",EDGE,{"disambiguationData":[OSD([sQuery(id+"F2.wireOp",EDGE,"E36.3")])],"isStart":true})});
            var Q5;
            Q5=makeQuery(id+"F3.boolean.opBoolean","COPY",EDGE,{"derivedFrom":makeQuery(id+"F3.opExtrude","CAP_EDGE",EDGE,{"disambiguationData":[OSD([sQuery(id+"F2.wireOp",EDGE,"E40.3")])],"isStart":true})});
            fillet(context, id + "F10", {"entities" : qUnion([Q0, Q1, Q2, Q3, Q4, Q5]), "radius" : 0.1 * mm, "tangentPropagation" : true, "allowEdgeOverflow" : false});
        }
        {
            var Q0;
            Q0=makeQuery(id+"F7.opExtrude","SWEPT_EDGE",EDGE,{"disambiguationData":[OSD([sQuery(id+"F0.wireOp",EDGE,"E16"),sQuery(id+"F0.wireOp",EDGE,"E25"),sQuery(id+"F6.wireOp",EDGE,"E51.3"),sQuery(id+"F6.wireOp",EDGE,"E53")])]});
            var Q1;
            Q1=makeQuery(id+"F7.opExtrude","SWEPT_EDGE",EDGE,{"disambiguationData":[OSD([sQuery(id+"F6.wireOp",EDGE,"E51.5"),sQuery(id+"F6.wireOp",EDGE,"E52")])]});
            fillet(context, id + "F11", {"entities" : qUnion([Q0, Q1]), "radius" : 0.5 * mm, "tangentPropagation" : true, "allowEdgeOverflow" : false});
        }
    });
